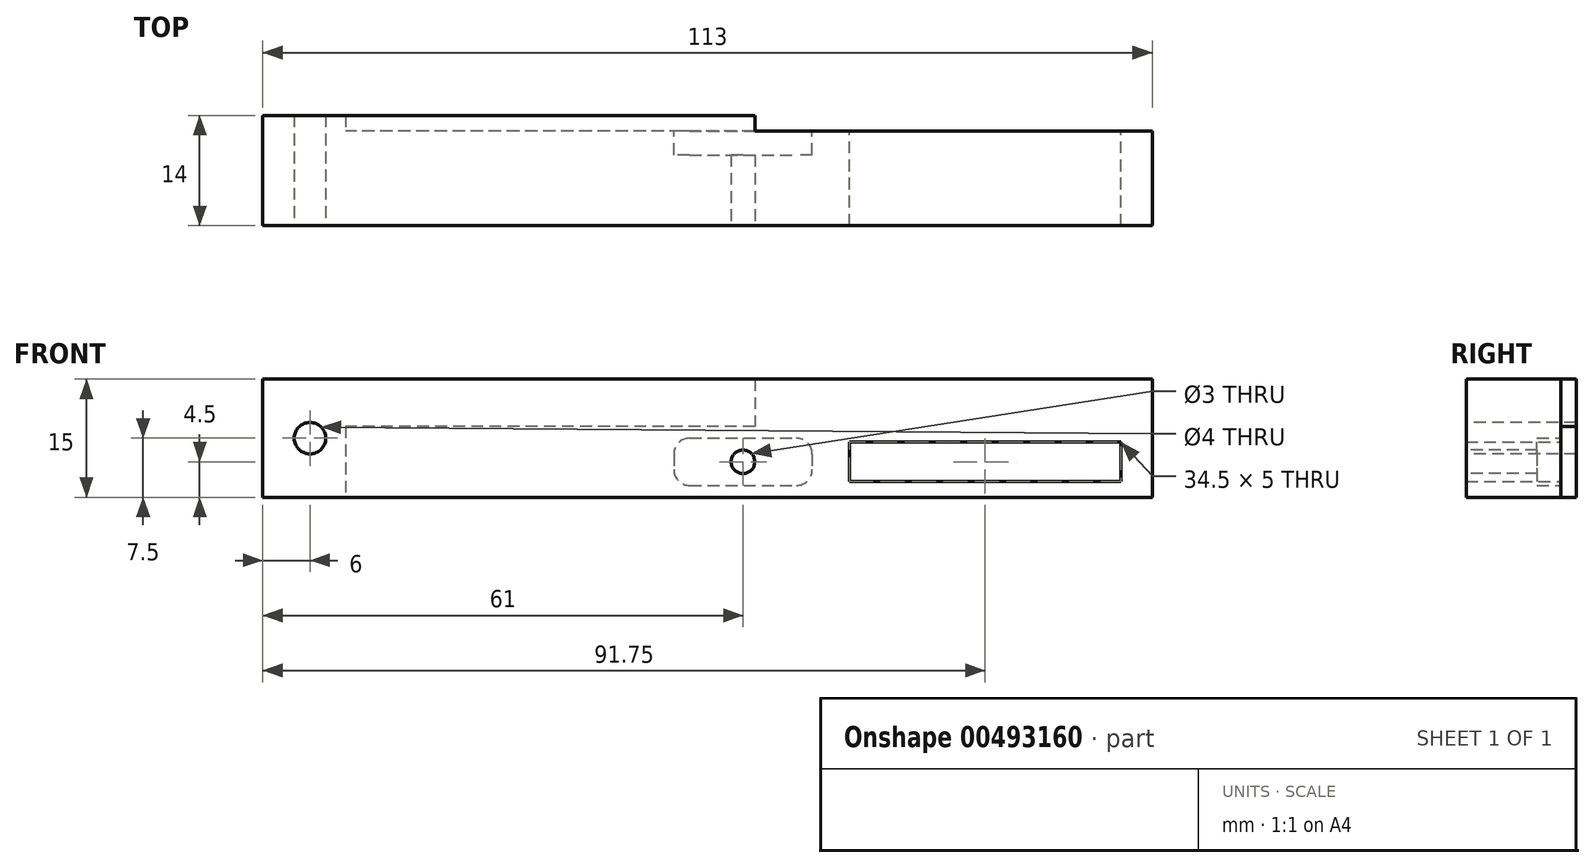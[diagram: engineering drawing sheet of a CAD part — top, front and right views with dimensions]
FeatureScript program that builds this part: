
annotation { "Feature Type Name" : "Feature", "Feature Type Description" : "" }
export const myFeature = defineFeature(function(context is Context, id is Id, definition is map)
    precondition{}
    {
        {
            var Q0;
            Q0=qCreatedBy(makeId("Front.planeOp"),FACE);
            var sketch = newSketch(context, id + "F0", { "sketchPlane" : qUnion([Q0])});
            skLineSegment(sketch, "E0.bottom", {"start": v(44, 7.5) * mm, "end": v(-44, 7.5) * mm});
            skLineSegment(sketch, "E0.top", {"start": v(44, -7.5) * mm, "end": v(-44, -7.5) * mm});
            skLineSegment(sketch, "E0.left", {"start": v(44, 7.5) * mm, "end": v(44, -7.5) * mm});
            skLineSegment(sketch, "E0.right", {"start": v(-44, 7.5) * mm, "end": v(-44, -7.5) * mm});
            skPoint(sketch, "E0.middle", {"position": v(0, 0) * mm});
            skSolve(sketch);
        }
        {
            var Q0;
            Q0 = qSketchRegion(id + "F0", true);
            extrude(context, id + "F1", {"entities" : qUnion([Q0]), "depth" : 14 * mm});
        }
        {
            var Q0;
            Q0=makeQuery(id+"F1.opExtrude","CAP_FACE",FACE,{"disambiguationData":[OSD([sQuery(id+"F0.wireOp",EDGE,"E0.bottom"),sQuery(id+"F0.wireOp",EDGE,"E0.top"),sQuery(id+"F0.wireOp",EDGE,"E0.left"),sQuery(id+"F0.wireOp",EDGE,"E0.right")])],"isStart":false});
            var sketch = newSketch(context, id + "F2", { "sketchPlane" : qUnion([Q0])});
            skLineSegment(sketch, "E1", {"start": v(-33.5, -7.5) * mm, "end": v(-33.5, 1.5) * mm});
            skLineSegment(sketch, "E2", {"start": v(-33.5, 1.5) * mm, "end": v(18.5, 1.5) * mm});
            skLineSegment(sketch, "E3", {"start": v(18.5, 1.5) * mm, "end": v(18.5, 7.5) * mm});
            skLineSegment(sketch, "E4", {"start": v(18.5, 7.5) * mm, "end": v(44, 7.5) * mm});
            skLineSegment(sketch, "E5", {"start": v(44, 7.5) * mm, "end": v(44, -7.5) * mm});
            skLineSegment(sketch, "E6", {"start": v(44, -7.5) * mm, "end": v(-33.5, -7.5) * mm});
            skSolve(sketch);
        }
        {
            var Q0;
            Q0 = qSketchRegion(id + "F2", true);
            extrude(context, id + "F3", {"entities" : qUnion([Q0]), "operationType" : NewBodyOperationType.REMOVE, "oppositeDirection" : true, "depth" : 24.5 * mm});
        }
        {
            var Q0;
            Q0=makeQuery(id+"F1.opExtrude","CAP_FACE",FACE,{"disambiguationData":[OSD([sQuery(id+"F0.wireOp",EDGE,"E0.bottom"),sQuery(id+"F0.wireOp",EDGE,"E0.top"),sQuery(id+"F0.wireOp",EDGE,"E0.left"),sQuery(id+"F0.wireOp",EDGE,"E0.right")])],"isStart":false});
            var sketch = newSketch(context, id + "F4", { "sketchPlane" : qUnion([Q0])});
            skLineSegment(sketch, "E7.bottom", {"start": v(-44, 7.5) * mm, "end": v(69, 7.5) * mm});
            skLineSegment(sketch, "E7.top", {"start": v(-44, -7.5) * mm, "end": v(69, -7.5) * mm});
            skLineSegment(sketch, "E7.left", {"start": v(-44, 7.5) * mm, "end": v(-44, -7.5) * mm});
            skLineSegment(sketch, "E7.right", {"start": v(69, 7.5) * mm, "end": v(69, -7.5) * mm});
            skSolve(sketch);
        }
        {
            var Q0;
            Q0 = qSketchRegion(id + "F4", true);
            extrude(context, id + "F5", {"entities" : qUnion([Q0]), "operationType" : NewBodyOperationType.ADD, "oppositeDirection" : true, "depth" : 12 * mm});
        }
        {
            var Q0;
            Q0=makeQuery(id+"F5.opExtrude","CAP_FACE",FACE,{"disambiguationData":[OSD([sQuery(id+"F4.wireOp",EDGE,"E7.bottom"),sQuery(id+"F4.wireOp",EDGE,"E7.top"),sQuery(id+"F4.wireOp",EDGE,"E7.left"),sQuery(id+"F4.wireOp",EDGE,"E7.right")])],"isStart":false});
            var sketch = newSketch(context, id + "F6", { "sketchPlane" : qUnion([Q0])});
            skLineSegment(sketch, "E8.bottom", {"start": v(-65, -0.5) * mm, "end": v(-30.5, -0.5) * mm});
            skLineSegment(sketch, "E8.top", {"start": v(-65, -5.5) * mm, "end": v(-30.5, -5.5) * mm});
            skLineSegment(sketch, "E8.left", {"start": v(-65, -0.5) * mm, "end": v(-65, -5.5) * mm});
            skLineSegment(sketch, "E8.right", {"start": v(-30.5, -0.5) * mm, "end": v(-30.5, -5.5) * mm});
            skSolve(sketch);
        }
        {
            var Q0;
            Q0 = qSketchRegion(id + "F6", true);
            extrude(context, id + "F7", {"entities" : qUnion([Q0]), "operationType" : NewBodyOperationType.REMOVE, "oppositeDirection" : true, "depth" : 25 * mm});
        }
        {
            var Q0;
            Q0=makeQuery(id+"F5.boolean.opBoolean","MERGE",FACE,{"derivedFrom":[makeQuery(id+"F1.opExtrude","CAP_FACE",FACE,{"disambiguationData":[OSD([sQuery(id+"F0.wireOp",EDGE,"E0.bottom"),sQuery(id+"F0.wireOp",EDGE,"E0.top"),sQuery(id+"F0.wireOp",EDGE,"E0.left"),sQuery(id+"F0.wireOp",EDGE,"E0.right")])],"isStart":false}),makeQuery(id+"F5.opExtrude","CAP_FACE",FACE,{"disambiguationData":[OSD([sQuery(id+"F4.wireOp",EDGE,"E7.bottom"),sQuery(id+"F4.wireOp",EDGE,"E7.top"),sQuery(id+"F4.wireOp",EDGE,"E7.left"),sQuery(id+"F4.wireOp",EDGE,"E7.right")])],"isStart":true})]});
            var sketch = newSketch(context, id + "F8", { "sketchPlane" : qUnion([Q0])});
            skCircle(sketch, "E9", {"center": v(17, -3) * mm, "radius": 1.5 * mm});
            skSolve(sketch);
        }
        {
            var Q0;
            Q0 = qSketchRegion(id + "F8", true);
            extrude(context, id + "F9", {"entities" : qUnion([Q0]), "operationType" : NewBodyOperationType.REMOVE, "oppositeDirection" : true, "depth" : 25 * mm});
        }
        {
            var Q0;
            Q0=makeQuery(id+"F5.opExtrude","CAP_FACE",FACE,{"disambiguationData":[OSD([sQuery(id+"F4.wireOp",EDGE,"E7.bottom"),sQuery(id+"F4.wireOp",EDGE,"E7.top"),sQuery(id+"F4.wireOp",EDGE,"E7.left"),sQuery(id+"F4.wireOp",EDGE,"E7.right")])],"isStart":false});
            var sketch = newSketch(context, id + "F10", { "sketchPlane" : qUnion([Q0])});
            skLineSegment(sketch, "E10.bottom", {"start": v(-8.2, 0) * mm, "end": v(-25.8, 0) * mm});
            skLineSegment(sketch, "E10.top", {"start": v(-8.2, -6) * mm, "end": v(-25.8, -6) * mm});
            skLineSegment(sketch, "E10.left", {"start": v(-8.2, 0) * mm, "end": v(-8.2, -6) * mm});
            skLineSegment(sketch, "E10.right", {"start": v(-25.8, 0) * mm, "end": v(-25.8, -6) * mm});
            skPoint(sketch, "E10.middle", {"position": v(-17, -3) * mm});
            skSolve(sketch);
        }
        {
            var Q0;
            Q0 = qSketchRegion(id + "F10", true);
            extrude(context, id + "F11", {"entities" : qUnion([Q0]), "operationType" : NewBodyOperationType.REMOVE, "oppositeDirection" : true, "depth" : 3 * mm});
        }
        {
            var Q0;
            Q0=makeQuery(id+"F11.boolean.opBoolean","COPY",EDGE,{"derivedFrom":makeQuery(id+"F11.opExtrude","SWEPT_EDGE",EDGE,{"disambiguationData":[OSD([sQuery(id+"F10.wireOp",EDGE,"E10.bottom"),sQuery(id+"F10.wireOp",EDGE,"E10.left")])]})});
            var Q1;
            Q1=makeQuery(id+"F11.boolean.opBoolean","COPY",EDGE,{"derivedFrom":makeQuery(id+"F11.opExtrude","SWEPT_EDGE",EDGE,{"disambiguationData":[OSD([sQuery(id+"F10.wireOp",EDGE,"E10.top"),sQuery(id+"F10.wireOp",EDGE,"E10.left")])]})});
            var Q2;
            Q2=makeQuery(id+"F11.boolean.opBoolean","COPY",EDGE,{"derivedFrom":makeQuery(id+"F11.opExtrude","SWEPT_EDGE",EDGE,{"disambiguationData":[OSD([sQuery(id+"F10.wireOp",EDGE,"E10.bottom"),sQuery(id+"F10.wireOp",EDGE,"E10.right")])]})});
            var Q3;
            Q3=makeQuery(id+"F11.boolean.opBoolean","COPY",EDGE,{"derivedFrom":makeQuery(id+"F11.opExtrude","SWEPT_EDGE",EDGE,{"disambiguationData":[OSD([sQuery(id+"F10.wireOp",EDGE,"E10.top"),sQuery(id+"F10.wireOp",EDGE,"E10.right")])]})});
            fillet(context, id + "F12", {"entities" : qUnion([Q0, Q1, Q2, Q3]), "radius" : 2 * mm, "tangentPropagation" : true, "allowEdgeOverflow" : false});
        }
        {
            var Q0;
            Q0=makeQuery(id+"F5.boolean.opBoolean","MERGE",FACE,{"derivedFrom":[makeQuery(id+"F1.opExtrude","CAP_FACE",FACE,{"disambiguationData":[OSD([sQuery(id+"F0.wireOp",EDGE,"E0.bottom"),sQuery(id+"F0.wireOp",EDGE,"E0.top"),sQuery(id+"F0.wireOp",EDGE,"E0.left"),sQuery(id+"F0.wireOp",EDGE,"E0.right")])],"isStart":false}),makeQuery(id+"F5.opExtrude","CAP_FACE",FACE,{"disambiguationData":[OSD([sQuery(id+"F4.wireOp",EDGE,"E7.bottom"),sQuery(id+"F4.wireOp",EDGE,"E7.top"),sQuery(id+"F4.wireOp",EDGE,"E7.left"),sQuery(id+"F4.wireOp",EDGE,"E7.right")])],"isStart":true})]});
            var sketch = newSketch(context, id + "F13", { "sketchPlane" : qUnion([Q0])});
            skCircle(sketch, "E11", {"center": v(-38, 0) * mm, "radius": 2 * mm});
            skSolve(sketch);
        }
        {
            var Q0;
            Q0 = qSketchRegion(id + "F13", true);
            extrude(context, id + "F14", {"entities" : qUnion([Q0]), "operationType" : NewBodyOperationType.REMOVE, "oppositeDirection" : true, "depth" : 25 * mm});
        }
    });
